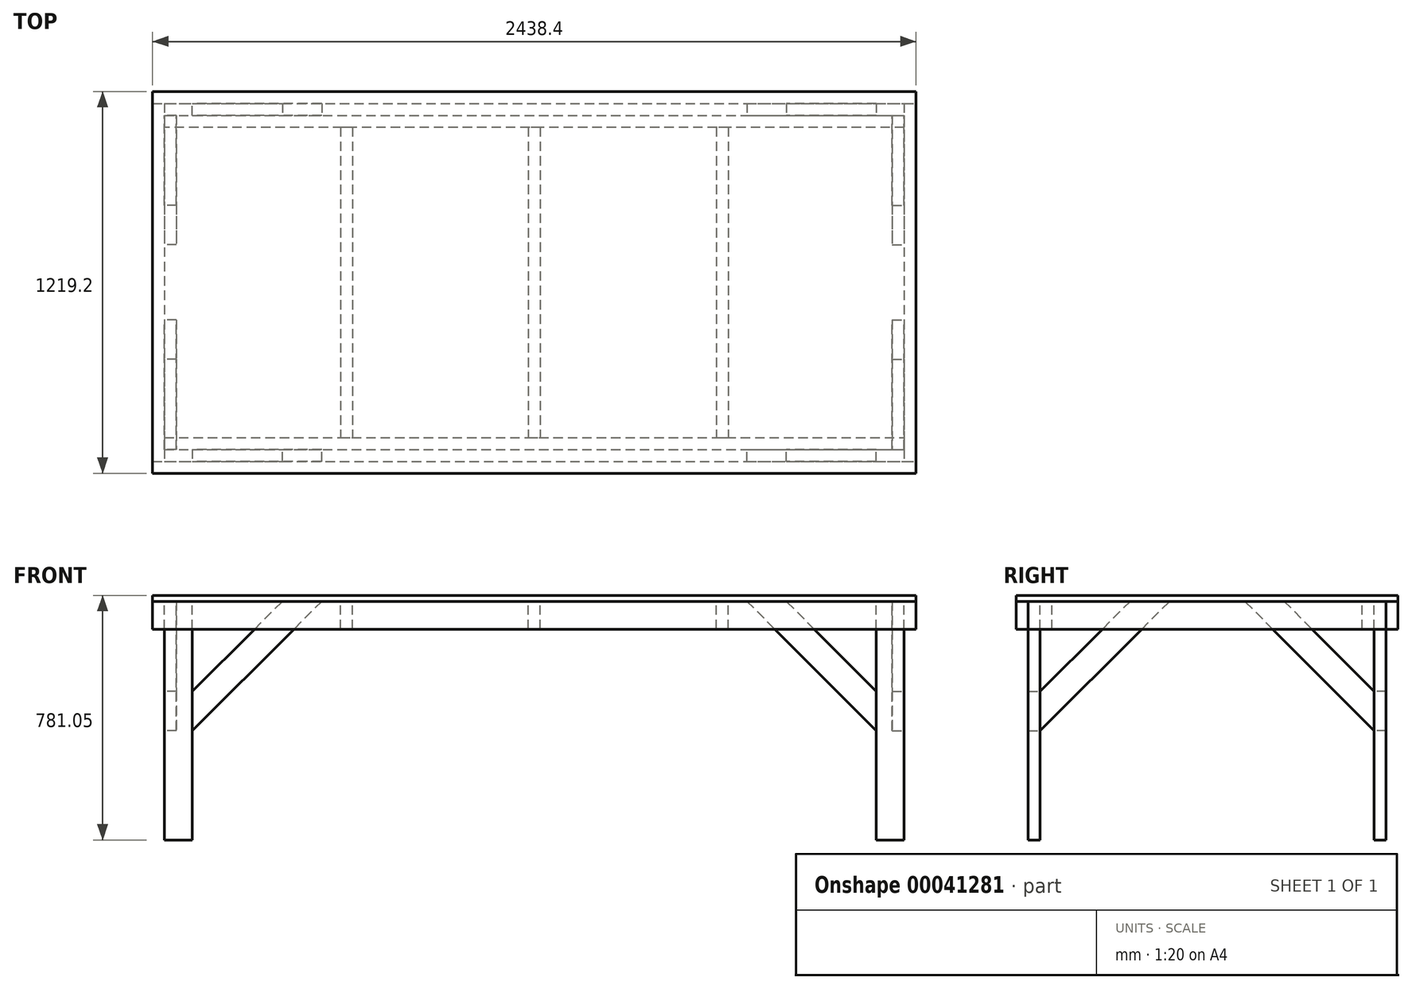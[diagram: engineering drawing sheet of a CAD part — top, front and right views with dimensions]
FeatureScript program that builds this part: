
annotation { "Feature Type Name" : "Feature", "Feature Type Description" : "" }
export const myFeature = defineFeature(function(context is Context, id is Id, definition is map)
    precondition{}
    {
        {
            var Q0;
            Q0=qCreatedBy(makeId("Top.planeOp"),FACE);
            var sketch = newSketch(context, id + "F0", { "sketchPlane" : qUnion([Q0])});
            skLineSegment(sketch, "E0.rect.bottom", {"start": v(1219.2, -609.6) * mm, "end": v(-1219.2, -609.6) * mm});
            skLineSegment(sketch, "E0.rect.top", {"start": v(1219.2, 609.6) * mm, "end": v(-1219.2, 609.6) * mm});
            skLineSegment(sketch, "E0.rect.left", {"start": v(1219.2, -609.6) * mm, "end": v(1219.2, 609.6) * mm});
            skLineSegment(sketch, "E0.rect.right", {"start": v(-1219.2, -609.6) * mm, "end": v(-1219.2, 609.6) * mm});
            skPoint(sketch, "E0.rect.middle", {"position": v(0, 0) * mm});
            skLineSegment(sketch, "E1", {"start": v(-1219.2, 571.5) * mm, "end": v(1219.2, 571.5) * mm});
            skLineSegment(sketch, "E2", {"start": v(-1219.2, -571.5) * mm, "end": v(1219.2, -571.5) * mm});
            skLineSegment(sketch, "E3", {"start": v(-1181.1, 571.5) * mm, "end": v(-1181.1, -571.5) * mm});
            skLineSegment(sketch, "E4", {"start": v(1181.1, 571.5) * mm, "end": v(1181.1, -571.5) * mm});
            skLineSegment(sketch, "E5", {"start": v(-1181.1, 533.4) * mm, "end": v(1181.1, 533.4) * mm});
            skLineSegment(sketch, "E6", {"start": v(-1181.1, -533.4) * mm, "end": v(1181.1, -533.4) * mm});
            skLineSegment(sketch, "E7", {"start": v(-1181.1, -495.3) * mm, "end": v(1181.1, -495.3) * mm});
            skLineSegment(sketch, "E8", {"start": v(1181.1, 495.3) * mm, "end": v(-1181.1, 495.3) * mm});
            skLineSegment(sketch, "E9", {"start": v(-1092.2, 533.4) * mm, "end": v(-1092.2, 571.5) * mm});
            skLineSegment(sketch, "E10", {"start": v(1092.2, 571.5) * mm, "end": v(1092.2, 533.4) * mm});
            skLineSegment(sketch, "E11", {"start": v(1092.2, -533.4) * mm, "end": v(1092.2, -571.5) * mm});
            skLineSegment(sketch, "E12", {"start": v(-1092.2, -533.4) * mm, "end": v(-1092.2, -571.5) * mm});
            skLineSegment(sketch, "E13", {"start": v(-619.13, 495.3) * mm, "end": v(-619.12, -495.3) * mm});
            skLineSegment(sketch, "E14", {"start": v(-581.03, 495.3) * mm, "end": v(-581.02, -495.3) * mm});
            skLineSegment(sketch, "E15", {"start": v(581.02, 495.3) * mm, "end": v(581.03, -495.3) * mm});
            skLineSegment(sketch, "E16", {"start": v(619.12, 495.3) * mm, "end": v(619.12, -495.3) * mm});
            skLineSegment(sketch, "E17", {"start": v(-19.05, 495.3) * mm, "end": v(-19.05, -495.3) * mm});
            skLineSegment(sketch, "E18", {"start": v(19.05, 495.3) * mm, "end": v(19.05, -495.3) * mm});
            skLineSegment(sketch, "E19", {"start": v(-619.13, 0) * mm, "end": v(-581.02, 0) * mm, "construction": true});
            skLineSegment(sketch, "E20", {"start": v(-19.05, 0) * mm, "end": v(19.05, 0) * mm, "construction": true});
            skLineSegment(sketch, "E21", {"start": v(581.02, 0) * mm, "end": v(619.12, 0) * mm, "construction": true});
            skLineSegment(sketch, "E22", {"start": v(-1219.2, 0) * mm, "end": v(-1181.1, 0) * mm, "construction": true});
            skLineSegment(sketch, "E23", {"start": v(1181.1, 0) * mm, "end": v(1219.2, 0) * mm, "construction": true});
            skLineSegment(sketch, "E24", {"start": v(-1200.15, 0) * mm, "end": v(-600.08, 0) * mm, "construction": true});
            skLineSegment(sketch, "E25", {"start": v(-600.08, 0) * mm, "end": v(0, 0) * mm, "construction": true});
            skLineSegment(sketch, "E26", {"start": v(0, 0) * mm, "end": v(600.07, 0) * mm, "construction": true});
            skLineSegment(sketch, "E27", {"start": v(600.07, 0) * mm, "end": v(1200.15, 0) * mm, "construction": true});
            skSolve(sketch);
        }
        {
            var Q0;
            {var subQ7=sQuery(id+"F0.wireOp",EDGE,"E0.rect.top");Q0=makeQuery(id+"F0.imprint","IMPRINT",FACE,{"disambiguationData":[TD([[makeQuery(id+"F0.imprint","IMPRINT",EDGE,{"derivedFrom":subQ7}),1.0]])]});}
            var Q1;
            {var subQ2=sQuery(id+"F0.wireOp",EDGE,"E3");var subQ4=sQuery(id+"F0.wireOp",EDGE,"E5");var subQ7=makeQuery(id+"F0.imprint","INTERSECT",VERTEX,{"derivedFrom":[subQ2,subQ4]});Q1=makeQuery(id+"F0.imprint","IMPRINT",FACE,{"disambiguationData":[TD([[makeQuery(id+"F0.imprint","IMPRINT",EDGE,{"disambiguationData":[TD([[subQ7,-1.0]])],"derivedFrom":subQ2}),1.0]])]});}
            var Q2;
            {var subQ3=sQuery(id+"F0.wireOp",EDGE,"E6");var subQ6=sQuery(id+"F0.wireOp",EDGE,"E3");var subQ8=makeQuery(id+"F0.imprint","INTERSECT",VERTEX,{"derivedFrom":[subQ6,subQ3]});Q2=makeQuery(id+"F0.imprint","IMPRINT",FACE,{"disambiguationData":[TD([[makeQuery(id+"F0.imprint","IMPRINT",EDGE,{"disambiguationData":[TD([[subQ8,1.0]])],"derivedFrom":subQ6}),1.0]])]});}
            var Q3;
            {var subQ4=sQuery(id+"F0.wireOp",EDGE,"E0.rect.bottom");Q3=makeQuery(id+"F0.imprint","IMPRINT",FACE,{"disambiguationData":[TD([[makeQuery(id+"F0.imprint","IMPRINT",EDGE,{"derivedFrom":subQ4}),-1.0]])]});}
            extrude(context, id + "F1", {"entities" : qUnion([Q0, Q1, Q2, Q3]), "oppositeDirection" : true, "depth" : 88.9 * mm});
        }
        {
            var Q0;
            {var subQ7=sQuery(id+"F0.wireOp",EDGE,"E1");var subQ9=sQuery(id+"F0.wireOp",EDGE,"E0.rect.right");var subQ10=makeQuery(id+"F0.imprint","INTERSECT",VERTEX,{"derivedFrom":[subQ9,subQ7]});Q0=makeQuery(id+"F0.imprint","IMPRINT",FACE,{"disambiguationData":[TD([[makeQuery(id+"F0.imprint","IMPRINT",EDGE,{"disambiguationData":[TD([[subQ10,1.0]])],"derivedFrom":subQ9}),-1.0]])]});}
            var Q1;
            {var subQ2=sQuery(id+"F0.wireOp",EDGE,"E13");Q1=makeQuery(id+"F0.imprint","IMPRINT",FACE,{"disambiguationData":[TD([[makeQuery(id+"F0.imprint","IMPRINT",EDGE,{"derivedFrom":subQ2}),1.0]])]});}
            var Q2;
            {var subQ0=sQuery(id+"F0.wireOp",EDGE,"E17");Q2=makeQuery(id+"F0.imprint","IMPRINT",FACE,{"disambiguationData":[TD([[makeQuery(id+"F0.imprint","IMPRINT",EDGE,{"derivedFrom":subQ0}),1.0]])]});}
            var Q3;
            {var subQ2=sQuery(id+"F0.wireOp",EDGE,"E15");Q3=makeQuery(id+"F0.imprint","IMPRINT",FACE,{"disambiguationData":[TD([[makeQuery(id+"F0.imprint","IMPRINT",EDGE,{"derivedFrom":subQ2}),1.0]])]});}
            var Q4;
            {var subQ6=sQuery(id+"F0.wireOp",EDGE,"E0.rect.left");var subQ8=sQuery(id+"F0.wireOp",EDGE,"E1");var subQ9=makeQuery(id+"F0.imprint","INTERSECT",VERTEX,{"derivedFrom":[subQ6,subQ8]});Q4=makeQuery(id+"F0.imprint","IMPRINT",FACE,{"disambiguationData":[TD([[makeQuery(id+"F0.imprint","IMPRINT",EDGE,{"disambiguationData":[TD([[subQ9,1.0]])],"derivedFrom":subQ6}),1.0]])]});}
            extrude(context, id + "F2", {"entities" : qUnion([Q0, Q1, Q2, Q3, Q4]), "oppositeDirection" : true, "depth" : 88.9 * mm});
        }
        {
            var Q0;
            {var subQ1=sQuery(id+"F0.wireOp",EDGE,"E9");Q0=makeQuery(id+"F0.imprint","IMPRINT",FACE,{"disambiguationData":[TD([[makeQuery(id+"F0.imprint","IMPRINT",EDGE,{"derivedFrom":subQ1}),1.0]])]});}
            var Q1;
            {var subQ1=sQuery(id+"F0.wireOp",EDGE,"E12");Q1=makeQuery(id+"F0.imprint","IMPRINT",FACE,{"disambiguationData":[TD([[makeQuery(id+"F0.imprint","IMPRINT",EDGE,{"derivedFrom":subQ1}),-1.0]])]});}
            var Q2;
            {var subQ0=sQuery(id+"F0.wireOp",EDGE,"E10");Q2=makeQuery(id+"F0.imprint","IMPRINT",FACE,{"disambiguationData":[TD([[makeQuery(id+"F0.imprint","IMPRINT",EDGE,{"derivedFrom":subQ0}),1.0]])]});}
            var Q3;
            {var subQ0=sQuery(id+"F0.wireOp",EDGE,"E11");Q3=makeQuery(id+"F0.imprint","IMPRINT",FACE,{"disambiguationData":[TD([[makeQuery(id+"F0.imprint","IMPRINT",EDGE,{"derivedFrom":subQ0}),1.0]])]});}
            extrude(context, id + "F3", {"entities" : qUnion([Q0, Q1, Q2, Q3]), "oppositeDirection" : true, "depth" : 762 * mm});
        }
        {
            var Q0;
            Q0=qCreatedBy(makeId("Top.planeOp"),FACE);
            var sketch = newSketch(context, id + "F4", { "sketchPlane" : qUnion([Q0])});
            skLineSegment(sketch, "E28.bottom", {"start": v(-1219.2, 609.6) * mm, "end": v(1219.2, 609.6) * mm});
            skLineSegment(sketch, "E28.top", {"start": v(-1219.2, -609.6) * mm, "end": v(1219.2, -609.6) * mm});
            skLineSegment(sketch, "E28.left", {"start": v(-1219.2, 609.6) * mm, "end": v(-1219.2, -609.6) * mm});
            skLineSegment(sketch, "E28.right", {"start": v(1219.2, 609.6) * mm, "end": v(1219.2, -609.6) * mm});
            skSolve(sketch);
        }
        {
            var Q0;
            Q0=makeQuery(id+"F4.imprint","IMPRINT",FACE,{"disambiguationData":[TD([[makeQuery(id+"F4.imprint","IMPRINT",EDGE,{"derivedFrom":sQuery(id+"F4.wireOp",EDGE,"E28.bottom")}),-1.0]])]});
            var sketch = newSketch(context, id + "F5", { "sketchPlane" : qUnion([Q0])});
            skSolve(sketch);
        }
        {
            var Q0;
            Q0=makeQuery(id+"F5.imprint","IMPRINT",FACE,{"disambiguationData":[TD([[makeQuery(id+"F5.imprint","IMPRINT",EDGE,{"derivedFrom":makeQuery(id+"F4.imprint","IMPRINT",EDGE,{"derivedFrom":sQuery(id+"F4.wireOp",EDGE,"E28.bottom")})}),-1.0]])]});
            extrude(context, id + "F12", {"entities" : qUnion([Q0]), "depth" : 19.05 * mm});
        }
        {
            var Q0;
            Q0=makeQuery(id+"F1.opExtrude","SWEPT_FACE",FACE,{"disambiguationData":[OSD([sQuery(id+"F0.wireOp",EDGE,"E6")])]});
            var sketch = newSketch(context, id + "F6", { "sketchPlane" : qUnion([Q0])});
            skLineSegment(sketch, "E29", {"start": v(-1092.2, -287.37) * mm, "end": v(-804.83, 0) * mm});
            skLineSegment(sketch, "E30", {"start": v(-804.83, 0) * mm, "end": v(-679.1, 0) * mm});
            skLineSegment(sketch, "E31", {"start": v(-679.1, 0) * mm, "end": v(-1092.2, -413.1) * mm});
            skLineSegment(sketch, "E32", {"start": v(-1092.2, -413.1) * mm, "end": v(-1092.2, -287.37) * mm});
            skLineSegment(sketch, "E33", {"start": v(0, -34.93) * mm, "end": v(0, -910.94) * mm, "construction": true});
            skLineSegment(sketch, "E34.MirrorCS", {"start": v(804.83, 0) * mm, "end": v(679.1, 0) * mm});
            skLineSegment(sketch, "E35.MirrorCS", {"start": v(679.1, 0) * mm, "end": v(1092.2, -413.1) * mm});
            skLineSegment(sketch, "E36.MirrorCS", {"start": v(1092.2, -413.1) * mm, "end": v(1092.2, -287.37) * mm});
            skLineSegment(sketch, "E37.MirrorCS", {"start": v(1092.2, -287.37) * mm, "end": v(804.83, 0) * mm});
            skSolve(sketch);
        }
        {
            var Q0;
            Q0 = qSketchRegion(id + "F6", true);
            extrude(context, id + "F7", {"entities" : qUnion([Q0]), "depth" : 38.1 * mm});
        }
        {
            var Q0;
            Q0=makeQuery(id+"F7.opExtrude","SWEPT_BODY",BODY,{"disambiguationData":[OSD([sQuery(id+"F6.wireOp",EDGE,"E29"),sQuery(id+"F6.wireOp",EDGE,"E30"),sQuery(id+"F6.wireOp",EDGE,"E31"),sQuery(id+"F6.wireOp",EDGE,"E32")])]});
            var Q1;
            Q1=makeQuery(id+"F7.opExtrude","SWEPT_BODY",BODY,{"disambiguationData":[OSD([sQuery(id+"F6.wireOp",EDGE,"E34.MirrorCS"),sQuery(id+"F6.wireOp",EDGE,"E35.MirrorCS"),sQuery(id+"F6.wireOp",EDGE,"E36.MirrorCS"),sQuery(id+"F6.wireOp",EDGE,"E37.MirrorCS")])]});
            var Q2;
            Q2=qCreatedBy(makeId("Front.planeOp"),FACE);
            mirror(context, id + "F8", {"entities" : qUnion([Q0, Q1]), "mirrorPlane" : qUnion([Q2])});
        }
        {
            var Q0;
            Q0=makeQuery(id+"F2.opExtrude","SWEPT_FACE",FACE,{"disambiguationData":[OSD([sQuery(id+"F0.wireOp",EDGE,"E3")])]});
            var sketch = newSketch(context, id + "F9", { "sketchPlane" : qUnion([Q0])});
            skLineSegment(sketch, "E38", {"start": v(-246.03, 0) * mm, "end": v(-533.4, -287.37) * mm});
            skLineSegment(sketch, "E39", {"start": v(-533.4, -287.37) * mm, "end": v(-533.4, -413.1) * mm});
            skLineSegment(sketch, "E40", {"start": v(-533.4, -413.1) * mm, "end": v(-120.3, 0) * mm});
            skLineSegment(sketch, "E41", {"start": v(-120.3, 0) * mm, "end": v(-246.03, 0) * mm});
            skLineSegment(sketch, "E42", {"start": v(0, 0) * mm, "end": v(0, -737.15) * mm, "construction": true});
            skPoint(sketch, "E42.endSnap0", {"position": v(0, -88.9) * mm});
            skLineSegment(sketch, "E43.MirrorCS", {"start": v(246.03, 0) * mm, "end": v(533.4, -287.37) * mm});
            skLineSegment(sketch, "E44.MirrorCS", {"start": v(533.4, -287.37) * mm, "end": v(533.4, -413.1) * mm});
            skLineSegment(sketch, "E45.MirrorCS", {"start": v(120.3, 0) * mm, "end": v(246.03, 0) * mm});
            skLineSegment(sketch, "E46.MirrorCS", {"start": v(533.4, -413.1) * mm, "end": v(120.3, 0) * mm});
            skSolve(sketch);
        }
        {
            var Q0;
            Q0 = qSketchRegion(id + "F9", true);
            extrude(context, id + "F10", {"entities" : qUnion([Q0]), "depth" : 38.1 * mm});
        }
        {
            var Q0;
            Q0=makeQuery(id+"F10.opExtrude","SWEPT_BODY",BODY,{"disambiguationData":[OSD([sQuery(id+"F9.wireOp",EDGE,"E38"),sQuery(id+"F9.wireOp",EDGE,"E39"),sQuery(id+"F9.wireOp",EDGE,"E40"),sQuery(id+"F9.wireOp",EDGE,"E41")])]});
            var Q1;
            Q1=makeQuery(id+"F10.opExtrude","SWEPT_BODY",BODY,{"disambiguationData":[OSD([sQuery(id+"F9.wireOp",EDGE,"E43.MirrorCS"),sQuery(id+"F9.wireOp",EDGE,"E44.MirrorCS"),sQuery(id+"F9.wireOp",EDGE,"E45.MirrorCS"),sQuery(id+"F9.wireOp",EDGE,"E46.MirrorCS")])]});
            var Q2;
            Q2=qCreatedBy(makeId("Right.planeOp"),FACE);
            mirror(context, id + "F11", {"entities" : qUnion([Q0, Q1]), "mirrorPlane" : qUnion([Q2])});
        }
    });
